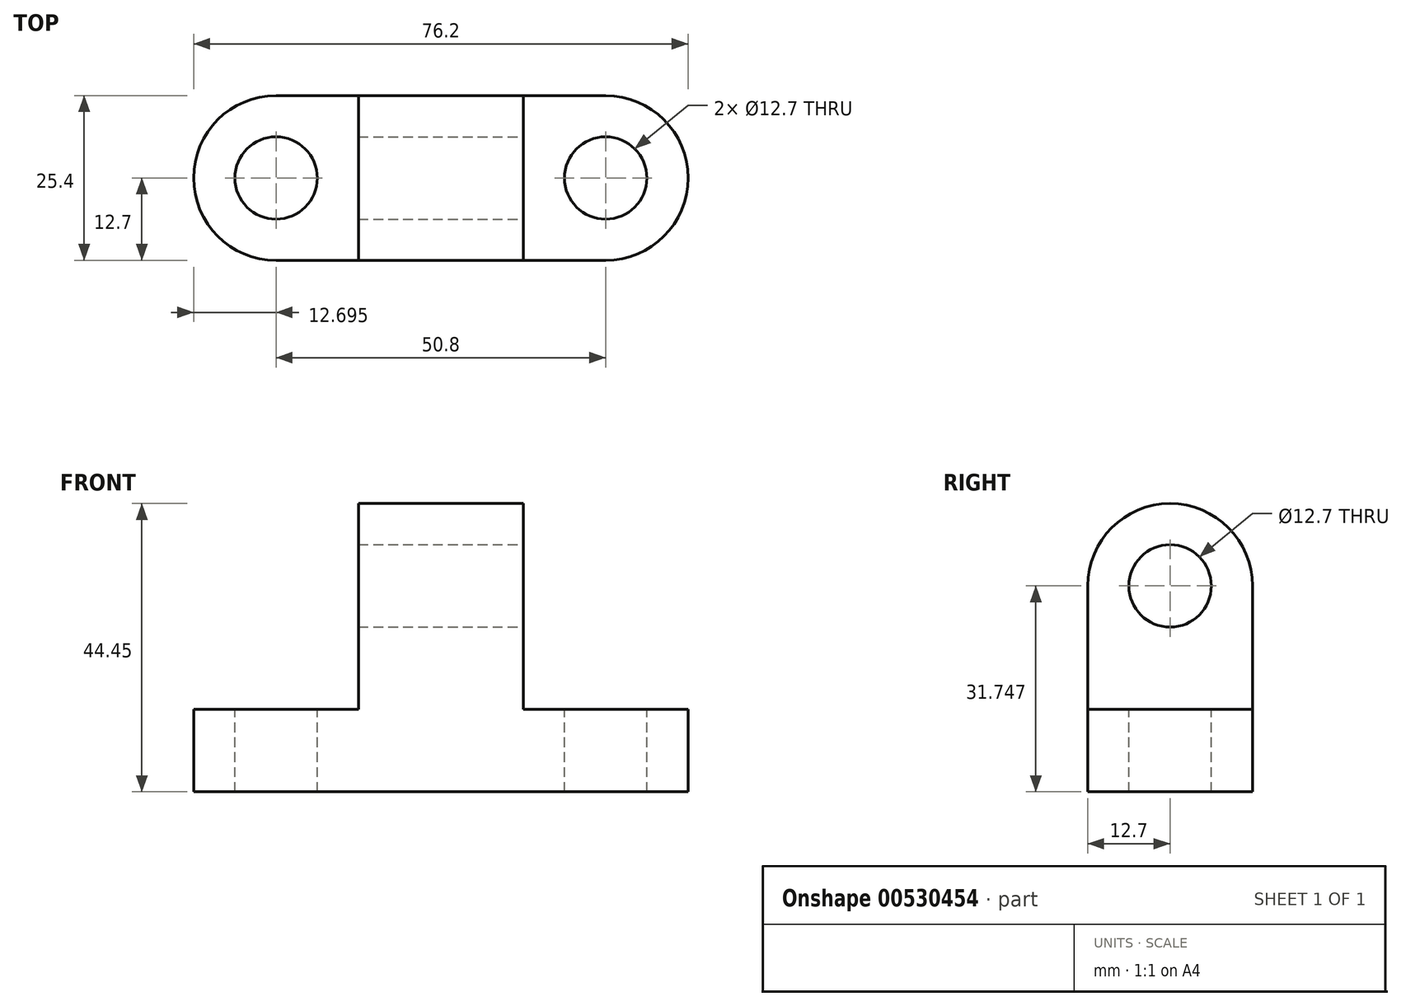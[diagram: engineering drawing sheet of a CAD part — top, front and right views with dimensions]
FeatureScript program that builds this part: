
annotation { "Feature Type Name" : "Feature", "Feature Type Description" : "" }
export const myFeature = defineFeature(function(context is Context, id is Id, definition is map)
    precondition{}
    {
        {
            var Q0;
            Q0=qCreatedBy(makeId("Front.planeOp"),FACE);
            var sketch = newSketch(context, id + "F0", { "sketchPlane" : qUnion([Q0])});
            skLineSegment(sketch, "E0", {"start": v(-51.07, 20.39) * mm, "end": v(25.13, 20.39) * mm});
            skLineSegment(sketch, "E1", {"start": v(25.13, 20.39) * mm, "end": v(25.13, 33.09) * mm});
            skLineSegment(sketch, "E2", {"start": v(25.13, 33.09) * mm, "end": v(-0.27, 33.09) * mm});
            skLineSegment(sketch, "E3", {"start": v(-0.27, 33.09) * mm, "end": v(-0.27, 64.84) * mm});
            skLineSegment(sketch, "E4", {"start": v(-0.27, 64.84) * mm, "end": v(-25.67, 64.84) * mm});
            skLineSegment(sketch, "E5", {"start": v(-25.67, 64.84) * mm, "end": v(-25.67, 33.09) * mm});
            skLineSegment(sketch, "E6", {"start": v(-25.67, 33.09) * mm, "end": v(-51.07, 33.09) * mm});
            skLineSegment(sketch, "E7", {"start": v(-51.07, 33.09) * mm, "end": v(-51.07, 20.39) * mm});
            skSolve(sketch);
        }
        {
            var Q0;
            Q0=makeQuery(id+"F0.imprint","IMPRINT",FACE,{"disambiguationData":[TD([[makeQuery(id+"F0.imprint","IMPRINT",EDGE,{"derivedFrom":sQuery(id+"F0.wireOp",EDGE,"E0")}),1.0]])]});
            extrude(context, id + "F1", {"entities" : qUnion([Q0]), "depth" : 25.4 * mm, "offsetDistance" : 25.4 * mm});
        }
        {
            var Q0;
            Q0=makeQuery(id+"F1.opExtrude","SWEPT_FACE",FACE,{"disambiguationData":[OSD([sQuery(id+"F0.wireOp",EDGE,"E6")])]});
            var sketch = newSketch(context, id + "F2", { "sketchPlane" : qUnion([Q0])});
            skArc(sketch, "E8", {"start": v(-38.37, 0) * mm, "mid": v(-51.07, -12.7) * mm, "end": v(-38.37, -25.4) * mm});
            skSolve(sketch);
        }
        {
            var Q0;
            {var subQ0=sQuery(id+"F2.wireOp",EDGE,"E8");var subQ1=sQuery(id+"F0.wireOp",EDGE,"E6");var subQ2=makeQuery(id+"F1.opExtrude","CAP_EDGE",EDGE,{"disambiguationData":[OSD([subQ1])],"isStart":true});var subQ3=makeQuery(id+"F2.imprint","INTERSECT",VERTEX,{"derivedFrom":[subQ2,subQ0]});Q0=makeQuery(id+"F2.imprint","IMPRINT",FACE,{"disambiguationData":[TD([[makeQuery(id+"F2.imprint","IMPRINT",EDGE,{"disambiguationData":[TD([[subQ3,-1.0]])],"derivedFrom":subQ0}),-1.0]])]});}
            var Q1;
            {var subQ0=sQuery(id+"F2.wireOp",EDGE,"E8");var subQ1=sQuery(id+"F0.wireOp",EDGE,"E6");var subQ2=makeQuery(id+"F1.opExtrude","CAP_EDGE",EDGE,{"disambiguationData":[OSD([subQ1])],"isStart":false});var subQ3=makeQuery(id+"F2.imprint","INTERSECT",VERTEX,{"derivedFrom":[subQ2,subQ0]});Q1=makeQuery(id+"F2.imprint","IMPRINT",FACE,{"disambiguationData":[TD([[makeQuery(id+"F2.imprint","IMPRINT",EDGE,{"disambiguationData":[TD([[subQ3,1.0]])],"derivedFrom":subQ0}),-1.0]])]});}
            extrude(context, id + "F3", {"entities" : qUnion([Q0, Q1]), "operationType" : NewBodyOperationType.REMOVE, "endBound" : BoundingType.THROUGH_ALL, "oppositeDirection" : true, "depth" : 25.4 * mm, "offsetDistance" : 25.4 * mm});
        }
        {
            var Q0;
            Q0=makeQuery(id+"F1.opExtrude","SWEPT_FACE",FACE,{"disambiguationData":[OSD([sQuery(id+"F0.wireOp",EDGE,"E2")])]});
            var sketch = newSketch(context, id + "F4", { "sketchPlane" : qUnion([Q0])});
            skArc(sketch, "E9", {"start": v(12.43, -25.4) * mm, "mid": v(25.13, -12.7) * mm, "end": v(12.43, 0) * mm});
            skSolve(sketch);
        }
        {
            var Q0;
            {var subQ0=sQuery(id+"F4.wireOp",EDGE,"E9");var subQ1=sQuery(id+"F0.wireOp",EDGE,"E2");var subQ2=makeQuery(id+"F1.opExtrude","CAP_EDGE",EDGE,{"disambiguationData":[OSD([subQ1])],"isStart":true});var subQ3=makeQuery(id+"F4.imprint","INTERSECT",VERTEX,{"derivedFrom":[subQ2,subQ0]});Q0=makeQuery(id+"F4.imprint","IMPRINT",FACE,{"disambiguationData":[TD([[makeQuery(id+"F4.imprint","IMPRINT",EDGE,{"disambiguationData":[TD([[subQ3,1.0]])],"derivedFrom":subQ0}),-1.0]])]});}
            var Q1;
            {var subQ0=sQuery(id+"F4.wireOp",EDGE,"E9");var subQ1=sQuery(id+"F0.wireOp",EDGE,"E2");var subQ2=makeQuery(id+"F1.opExtrude","CAP_EDGE",EDGE,{"disambiguationData":[OSD([subQ1])],"isStart":false});var subQ3=makeQuery(id+"F4.imprint","INTERSECT",VERTEX,{"derivedFrom":[subQ2,subQ0]});Q1=makeQuery(id+"F4.imprint","IMPRINT",FACE,{"disambiguationData":[TD([[makeQuery(id+"F4.imprint","IMPRINT",EDGE,{"disambiguationData":[TD([[subQ3,-1.0]])],"derivedFrom":subQ0}),-1.0]])]});}
            extrude(context, id + "F5", {"entities" : qUnion([Q0, Q1]), "operationType" : NewBodyOperationType.REMOVE, "endBound" : BoundingType.THROUGH_ALL, "oppositeDirection" : true, "depth" : 25.4 * mm, "offsetDistance" : 25.4 * mm});
        }
        {
            var Q0;
            Q0=makeQuery(id+"F1.opExtrude","SWEPT_FACE",FACE,{"disambiguationData":[OSD([sQuery(id+"F0.wireOp",EDGE,"E3")])]});
            var sketch = newSketch(context, id + "F6", { "sketchPlane" : qUnion([Q0])});
            skArc(sketch, "E10", {"start": v(0, 52.14) * mm, "mid": v(-12.7, 64.84) * mm, "end": v(-25.4, 52.14) * mm});
            skSolve(sketch);
        }
        {
            var Q0;
            {var subQ0=sQuery(id+"F6.wireOp",EDGE,"E10");var subQ1=sQuery(id+"F0.wireOp",EDGE,"E3");var subQ2=makeQuery(id+"F1.opExtrude","CAP_EDGE",EDGE,{"disambiguationData":[OSD([subQ1])],"isStart":false});var subQ3=makeQuery(id+"F6.imprint","INTERSECT",VERTEX,{"derivedFrom":[subQ2,subQ0]});Q0=makeQuery(id+"F6.imprint","IMPRINT",FACE,{"disambiguationData":[TD([[makeQuery(id+"F6.imprint","IMPRINT",EDGE,{"disambiguationData":[TD([[subQ3,1.0]])],"derivedFrom":subQ0}),-1.0]])]});}
            var Q1;
            {var subQ0=sQuery(id+"F6.wireOp",EDGE,"E10");var subQ1=sQuery(id+"F0.wireOp",EDGE,"E3");var subQ2=makeQuery(id+"F1.opExtrude","CAP_EDGE",EDGE,{"disambiguationData":[OSD([subQ1])],"isStart":true});var subQ3=makeQuery(id+"F6.imprint","INTERSECT",VERTEX,{"derivedFrom":[subQ2,subQ0]});Q1=makeQuery(id+"F6.imprint","IMPRINT",FACE,{"disambiguationData":[TD([[makeQuery(id+"F6.imprint","IMPRINT",EDGE,{"disambiguationData":[TD([[subQ3,-1.0]])],"derivedFrom":subQ0}),-1.0]])]});}
            extrude(context, id + "F7", {"entities" : qUnion([Q0, Q1]), "operationType" : NewBodyOperationType.REMOVE, "endBound" : BoundingType.THROUGH_ALL, "oppositeDirection" : true, "depth" : 25.4 * mm, "offsetDistance" : 25.4 * mm});
        }
        {
            var Q0;
            Q0=makeQuery(id+"F1.opExtrude","SWEPT_FACE",FACE,{"disambiguationData":[OSD([sQuery(id+"F0.wireOp",EDGE,"E3")])]});
            var sketch = newSketch(context, id + "F8", { "sketchPlane" : qUnion([Q0])});
            skCircle(sketch, "E11", {"center": v(-12.7, 52.14) * mm, "radius": 6.35 * mm});
            skSolve(sketch);
        }
        {
            var Q0;
            Q0=makeQuery(id+"F8.imprint","IMPRINT",FACE,{"disambiguationData":[TD([[makeQuery(id+"F8.imprint","IMPRINT",EDGE,{"derivedFrom":sQuery(id+"F8.wireOp",EDGE,"E11")}),1.0]])]});
            extrude(context, id + "F9", {"entities" : qUnion([Q0]), "operationType" : NewBodyOperationType.REMOVE, "endBound" : BoundingType.THROUGH_ALL, "oppositeDirection" : true, "depth" : 25.4 * mm, "offsetDistance" : 25.4 * mm});
        }
        {
            var Q0;
            Q0=makeQuery(id+"F1.opExtrude","SWEPT_FACE",FACE,{"disambiguationData":[OSD([sQuery(id+"F0.wireOp",EDGE,"E6")])]});
            var sketch = newSketch(context, id + "F10", { "sketchPlane" : qUnion([Q0])});
            skCircle(sketch, "E12", {"center": v(-38.37, -12.7) * mm, "radius": 6.35 * mm});
            skSolve(sketch);
        }
        {
            var Q0;
            Q0=makeQuery(id+"F10.imprint","IMPRINT",FACE,{"disambiguationData":[TD([[makeQuery(id+"F10.imprint","IMPRINT",EDGE,{"derivedFrom":sQuery(id+"F10.wireOp",EDGE,"E12")}),1.0]])]});
            extrude(context, id + "F11", {"entities" : qUnion([Q0]), "operationType" : NewBodyOperationType.REMOVE, "endBound" : BoundingType.THROUGH_ALL, "oppositeDirection" : true, "depth" : 25.4 * mm, "offsetDistance" : 25.4 * mm});
        }
        {
            var Q0;
            Q0=makeQuery(id+"F1.opExtrude","SWEPT_FACE",FACE,{"disambiguationData":[OSD([sQuery(id+"F0.wireOp",EDGE,"E2")])]});
            var sketch = newSketch(context, id + "F12", { "sketchPlane" : qUnion([Q0])});
            skCircle(sketch, "E13", {"center": v(12.43, -12.7) * mm, "radius": 6.35 * mm});
            skSolve(sketch);
        }
        {
            var Q0;
            Q0=makeQuery(id+"F12.imprint","IMPRINT",FACE,{"disambiguationData":[TD([[makeQuery(id+"F12.imprint","IMPRINT",EDGE,{"derivedFrom":sQuery(id+"F12.wireOp",EDGE,"E13")}),1.0]])]});
            extrude(context, id + "F13", {"entities" : qUnion([Q0]), "operationType" : NewBodyOperationType.REMOVE, "endBound" : BoundingType.THROUGH_ALL, "oppositeDirection" : true, "depth" : 25.4 * mm, "offsetDistance" : 25.4 * mm});
        }
    });
